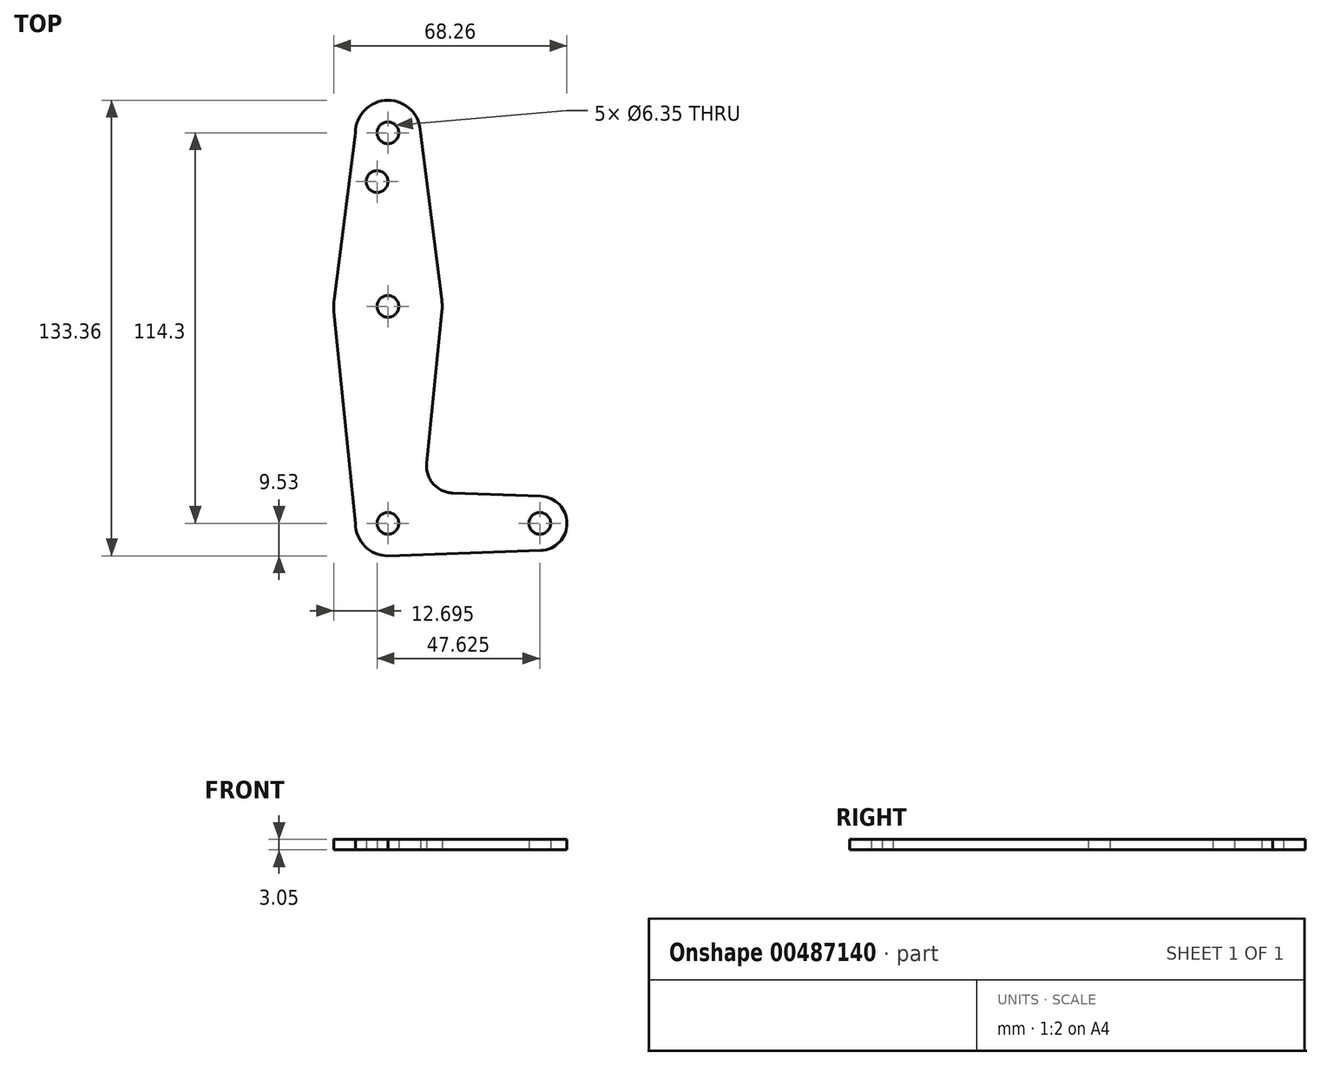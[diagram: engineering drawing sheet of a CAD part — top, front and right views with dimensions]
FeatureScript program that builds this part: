
annotation { "Feature Type Name" : "Feature", "Feature Type Description" : "" }
export const myFeature = defineFeature(function(context is Context, id is Id, definition is map)
    precondition{}
    {
        {
            var Q0;
            Q0=qCreatedBy(makeId("Top.planeOp"),FACE);
            var sketch = newSketch(context, id + "F0", { "sketchPlane" : qUnion([Q0])});
            skLineSegment(sketch, "E0", {"start": v(0, 0) * mm, "end": v(0, 114.3) * mm, "construction": true});
            skLineSegment(sketch, "E1", {"start": v(0, 0) * mm, "end": v(44.45, 0) * mm});
            skCircle(sketch, "E2", {"center": v(0, 0) * mm, "radius": 9.53 * mm});
            skCircle(sketch, "E3", {"center": v(44.45, 0) * mm, "radius": 7.94 * mm});
            skCircle(sketch, "E4", {"center": v(0, 114.3) * mm, "radius": 9.52 * mm});
            skCircle(sketch, "E5", {"center": v(0, 63.5) * mm, "radius": 15.88 * mm});
            skLineSegment(sketch, "E6", {"start": v(-9.52, 114.3) * mm, "end": v(-15.75, 65.5) * mm});
            skLineSegment(sketch, "E7", {"start": v(9.52, 114.3) * mm, "end": v(15.75, 65.5) * mm});
            skLineSegment(sketch, "E8", {"start": v(-9.53, 0) * mm, "end": v(-15.8, 61.9) * mm});
            skLineSegment(sketch, "E9", {"start": v(11.34, 17.6) * mm, "end": v(15.8, 61.91) * mm});
            skLineSegment(sketch, "E10", {"start": v(18.97, 8.85) * mm, "end": v(44.73, 7.93) * mm});
            skLineSegment(sketch, "E11", {"start": v(0, -9.53) * mm, "end": v(44.73, -7.93) * mm});
            skCircle(sketch, "E12", {"center": v(0, 114.3) * mm, "radius": 3.18 * mm});
            skCircle(sketch, "E13", {"center": v(0, 63.5) * mm, "radius": 3.18 * mm});
            skCircle(sketch, "E14", {"center": v(0, 0) * mm, "radius": 3.18 * mm});
            skCircle(sketch, "E15", {"center": v(44.45, 0) * mm, "radius": 3.18 * mm});
            skArc(sketch, "E16.filletArc", {"start": v(11.34, 17.6) * mm, "mid": v(13.26, 11.57) * mm, "end": v(18.97, 8.85) * mm});
            skCircle(sketch, "E17", {"center": v(-3.18, 100.03) * mm, "radius": 3.18 * mm});
            skSolve(sketch);
        }
        {
            var Q0;
            {var subQ1=sQuery(id+"F0.wireOp",EDGE,"E6");Q0=makeQuery(id+"F0.imprint","IMPRINT",FACE,{"disambiguationData":[TD([[makeQuery(id+"F0.imprint","IMPRINT",EDGE,{"derivedFrom":subQ1}),1.0]])]});}
            var Q1;
            Q1=makeQuery(id+"F0.imprint","IMPRINT",FACE,{"disambiguationData":[TD([[makeQuery(id+"F0.imprint","IMPRINT",EDGE,{"derivedFrom":sQuery(id+"F0.wireOp",EDGE,"E12")}),-1.0]])]});
            var Q2;
            Q2=makeQuery(id+"F0.imprint","IMPRINT",FACE,{"disambiguationData":[TD([[makeQuery(id+"F0.imprint","IMPRINT",EDGE,{"derivedFrom":sQuery(id+"F0.wireOp",EDGE,"E13")}),-1.0]])]});
            var Q3;
            {var subQ0=sQuery(id+"F0.wireOp",EDGE,"E8");Q3=makeQuery(id+"F0.imprint","IMPRINT",FACE,{"disambiguationData":[TD([[makeQuery(id+"F0.imprint","IMPRINT",EDGE,{"derivedFrom":subQ0}),-1.0]])]});}
            var Q4;
            {var subQ0=sQuery(id+"F0.wireOp",EDGE,"E2");var subQ1=sQuery(id+"F0.wireOp",EDGE,"E1");var subQ2=makeQuery(id+"F0.imprint","INTERSECT",VERTEX,{"derivedFrom":[subQ1,subQ0]});Q4=makeQuery(id+"F0.imprint","IMPRINT",FACE,{"disambiguationData":[TD([[makeQuery(id+"F0.imprint","IMPRINT",EDGE,{"disambiguationData":[TD([[subQ2,-1.0]])],"derivedFrom":subQ1}),-1.0]])]});}
            var Q5;
            Q5=makeQuery(id+"F0.imprint","IMPRINT",FACE,{"disambiguationData":[TD([[makeQuery(id+"F0.imprint","IMPRINT",EDGE,{"derivedFrom":sQuery(id+"F0.wireOp",EDGE,"E14")}),-1.0]])]});
            var Q6;
            Q6=makeQuery(id+"F0.imprint","IMPRINT",FACE,{"disambiguationData":[TD([[makeQuery(id+"F0.imprint","IMPRINT",EDGE,{"derivedFrom":sQuery(id+"F0.wireOp",EDGE,"E15")}),-1.0]])]});
            extrude(context, id + "F1", {"entities" : qUnion([Q0, Q1, Q2, Q3, Q4, Q5, Q6]), "depth" : 3.05 * mm});
        }
    });
